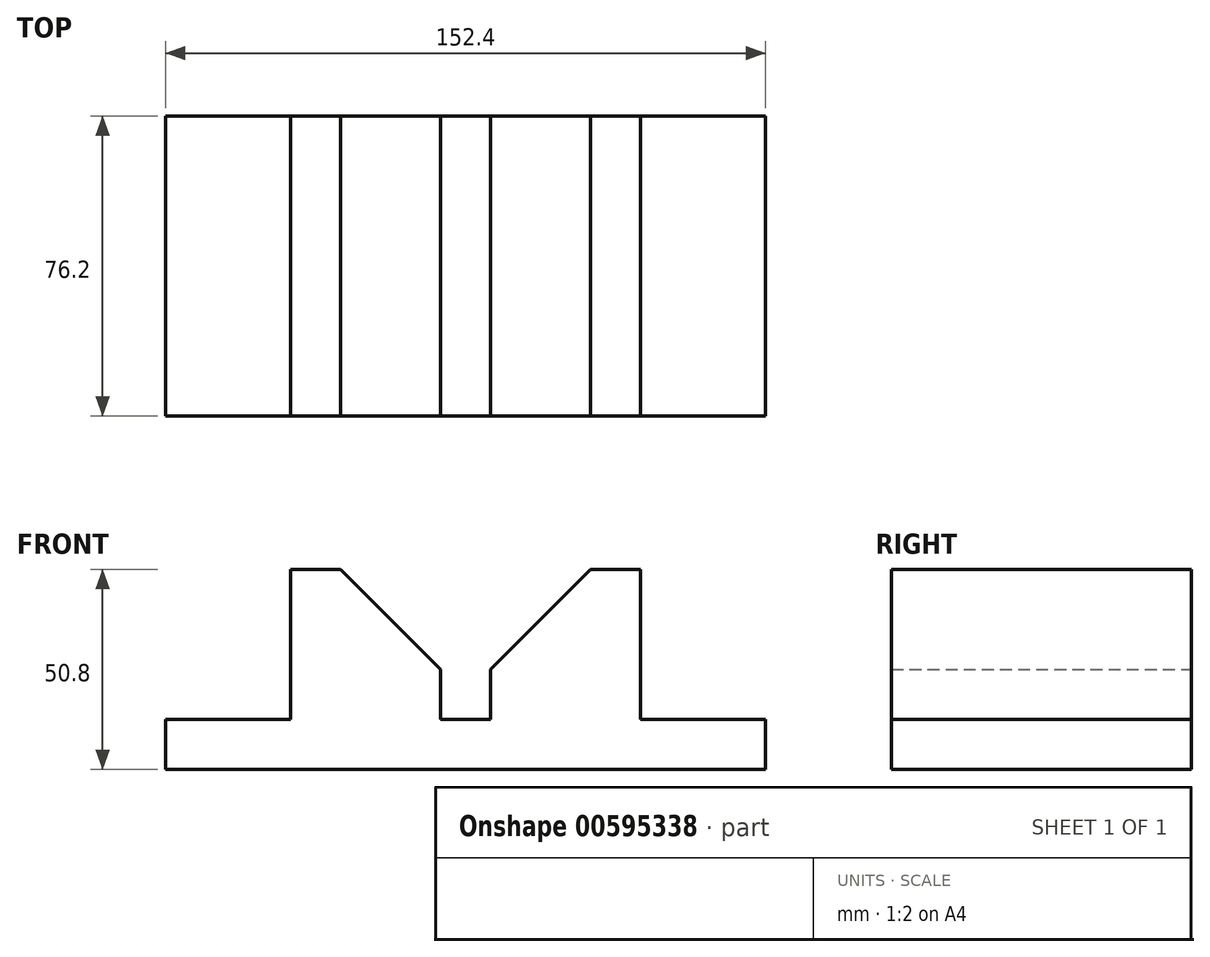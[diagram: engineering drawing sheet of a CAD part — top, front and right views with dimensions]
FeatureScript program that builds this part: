
annotation { "Feature Type Name" : "Feature", "Feature Type Description" : "" }
export const myFeature = defineFeature(function(context is Context, id is Id, definition is map)
    precondition{}
    {
        {
            var Q0;
            Q0=qCreatedBy(makeId("Front.planeOp"),FACE);
            var sketch = newSketch(context, id + "F0", { "sketchPlane" : qUnion([Q0])});
            skLineSegment(sketch, "E0.bottom", {"start": v(0, 0) * mm, "end": v(152.4, 0) * mm});
            skLineSegment(sketch, "E0.top", {"start": v(0, 50.8) * mm, "end": v(152.4, 50.8) * mm});
            skLineSegment(sketch, "E0.left", {"start": v(0, 0) * mm, "end": v(0, 50.8) * mm});
            skLineSegment(sketch, "E0.right", {"start": v(152.4, 0) * mm, "end": v(152.4, 50.8) * mm});
            skLineSegment(sketch, "E1", {"start": v(0, 12.7) * mm, "end": v(31.75, 12.7) * mm});
            skLineSegment(sketch, "E2", {"start": v(31.75, 12.7) * mm, "end": v(31.75, 50.8) * mm});
            skLineSegment(sketch, "E3", {"start": v(31.75, 50.8) * mm, "end": v(44.45, 50.8) * mm});
            skLineSegment(sketch, "E4", {"start": v(76.2, 12.7) * mm, "end": v(69.85, 12.7) * mm});
            skLineSegment(sketch, "E5", {"start": v(69.85, 12.7) * mm, "end": v(69.85, 25.4) * mm});
            skLineSegment(sketch, "E6", {"start": v(44.45, 50.8) * mm, "end": v(69.85, 25.4) * mm});
            skLineSegment(sketch, "E7.MirrorCS", {"start": v(76.2, 12.7) * mm, "end": v(82.55, 12.7) * mm});
            skLineSegment(sketch, "E8.MirrorCS", {"start": v(82.55, 12.7) * mm, "end": v(82.55, 25.4) * mm});
            skLineSegment(sketch, "E9.MirrorCS", {"start": v(107.95, 50.8) * mm, "end": v(82.55, 25.4) * mm});
            skLineSegment(sketch, "E10.MirrorCS", {"start": v(120.65, 50.8) * mm, "end": v(107.95, 50.8) * mm});
            skLineSegment(sketch, "E11.MirrorCS", {"start": v(120.65, 12.7) * mm, "end": v(120.65, 50.8) * mm});
            skLineSegment(sketch, "E12.MirrorCS", {"start": v(152.4, 12.7) * mm, "end": v(120.65, 12.7) * mm});
            skSolve(sketch);
        }
        {
            var Q0;
            {var subQ0=sQuery(id+"F0.wireOp",EDGE,"E0.bottom");Q0=makeQuery(id+"F0.imprint","IMPRINT",FACE,{"disambiguationData":[TD([[makeQuery(id+"F0.imprint","IMPRINT",EDGE,{"derivedFrom":subQ0}),1.0]])]});}
            extrude(context, id + "F1", {"entities" : qUnion([Q0]), "depth" : 76.2 * mm, "offsetDistance" : 25.4 * mm});
        }
    });
